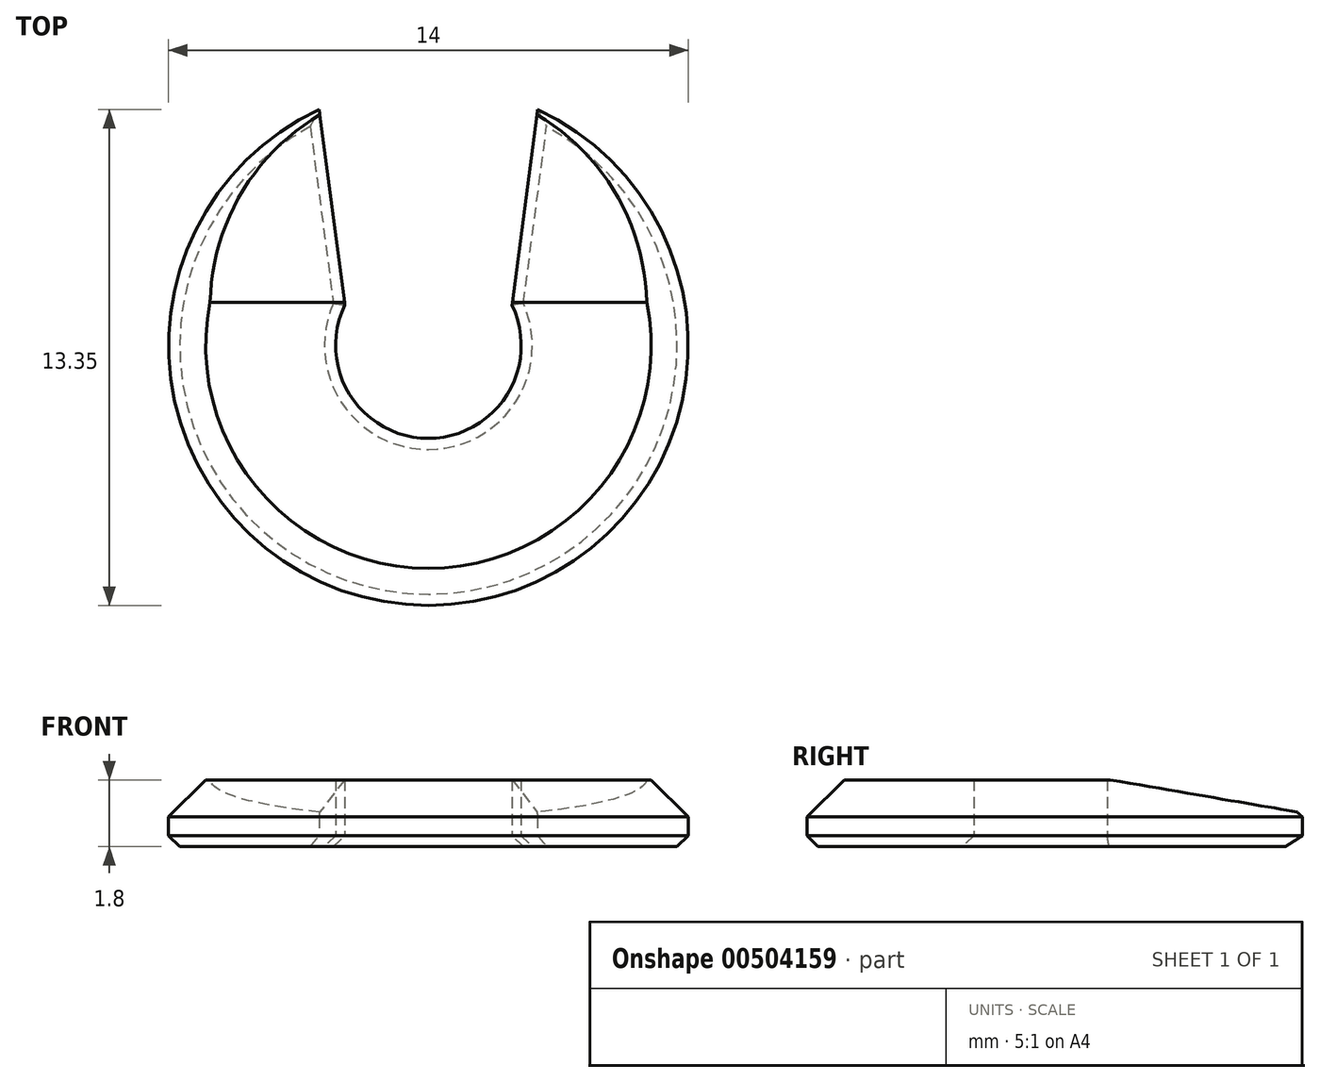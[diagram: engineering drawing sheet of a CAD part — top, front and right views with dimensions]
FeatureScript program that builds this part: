
annotation { "Feature Type Name" : "Feature", "Feature Type Description" : "" }
export const myFeature = defineFeature(function(context is Context, id is Id, definition is map)
    precondition{}
    {
        {
            var Q0;
            Q0=qCreatedBy(makeId("Top.planeOp"),FACE);
            var sketch = newSketch(context, id + "F0", { "sketchPlane" : qUnion([Q0])});
            skCircle(sketch, "E0", {"center": v(0, 0) * mm, "radius": 2.5 * mm});
            skCircle(sketch, "E1", {"center": v(0, 0) * mm, "radius": 7 * mm});
            skLineSegment(sketch, "E2", {"start": v(-2.25, 1.09) * mm, "end": v(-2.94, 6.35) * mm});
            skLineSegment(sketch, "E3", {"start": v(2.25, 1.09) * mm, "end": v(2.94, 6.35) * mm});
            skSolve(sketch);
        }
        {
            var Q0;
            {var subQ0=sQuery(id+"F0.wireOp",EDGE,"E2");Q0=makeQuery(id+"F0.imprint","IMPRINT",FACE,{"disambiguationData":[TD([[makeQuery(id+"F0.imprint","IMPRINT",EDGE,{"derivedFrom":subQ0}),1.0]])]});}
            extrude(context, id + "F1", {"entities" : qUnion([Q0]), "depth" : 1.8 * mm});
        }
        {
            var Q0;
            Q0=qCreatedBy(makeId("Right.planeOp"),FACE);
            var sketch = newSketch(context, id + "F2", { "sketchPlane" : qUnion([Q0])});
            skLineSegment(sketch, "E4", {"start": v(7, 0.8) * mm, "end": v(0, 2) * mm});
            skLineSegment(sketch, "E5", {"start": v(0, 2) * mm, "end": v(0, 10.1) * mm});
            skLineSegment(sketch, "E6", {"start": v(0, 10.1) * mm, "end": v(7, 10.1) * mm});
            skLineSegment(sketch, "E7", {"start": v(7, 10.1) * mm, "end": v(7, 0.8) * mm});
            skSolve(sketch);
        }
        {
            var Q0;
            Q0=makeQuery(id+"F2.imprint","IMPRINT",FACE,{"disambiguationData":[TD([[makeQuery(id+"F2.imprint","IMPRINT",EDGE,{"derivedFrom":sQuery(id+"F2.wireOp",EDGE,"E4")}),-1.0]])]});
            extrude(context, id + "F3", {"entities" : qUnion([Q0]), "operationType" : NewBodyOperationType.REMOVE, "oppositeDirection" : true, "depth" : 25 * mm, "hasSecondDirection" : true, "secondDirectionOppositeDirection" : false, "secondDirectionDepth" : 25 * mm});
        }
        {
            var Q0;
            Q0=makeQuery(id+"F1.opExtrude","CAP_EDGE",EDGE,{"disambiguationData":[OSD([sQuery(id+"F0.wireOp",EDGE,"E1")])],"isStart":false});
            chamfer(context, id + "F4", {"entities" : qUnion([Q0]), "width" : 1 * mm, "tangentPropagation" : true});
        }
        {
            var Q0;
            Q0=makeQuery(id+"F1.opExtrude","CAP_FACE",FACE,{"disambiguationData":[OSD([sQuery(id+"F0.wireOp",EDGE,"E0"),sQuery(id+"F0.wireOp",EDGE,"E1"),sQuery(id+"F0.wireOp",EDGE,"E2"),sQuery(id+"F0.wireOp",EDGE,"E3")])],"isStart":true});
            chamfer(context, id + "F5", {"entities" : qUnion([Q0]), "width" : .3 * mm, "tangentPropagation" : true});
        }
    });
